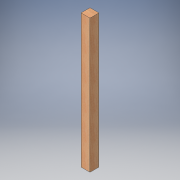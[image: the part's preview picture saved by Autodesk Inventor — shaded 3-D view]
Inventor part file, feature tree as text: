
AUTODESK INVENTOR PART (.ipt)
format: ipt  version: 2016 (Build 200138000, 138)  size: 95,744 bytes
history: native  units: in
note: dims shown in document units (in); Inventor stores cm internally (conversion verified against a paired STEP export)
features: extrude x1, sketch x1
ambient origin geometry x8: Origin, YZ Plane, XZ Plane, XY Plane, X Axis, Y Axis, Z Axis, Center Point
bodies: Solid1 (feature_tree)
feature tree (2):
  extrude  "Extrusion1"  Depth=52.25in TaperAngle=0.0deg
  sketch  "Sketch1"  dims[d0=3.5in d1=52.25in d2=0.0in]
